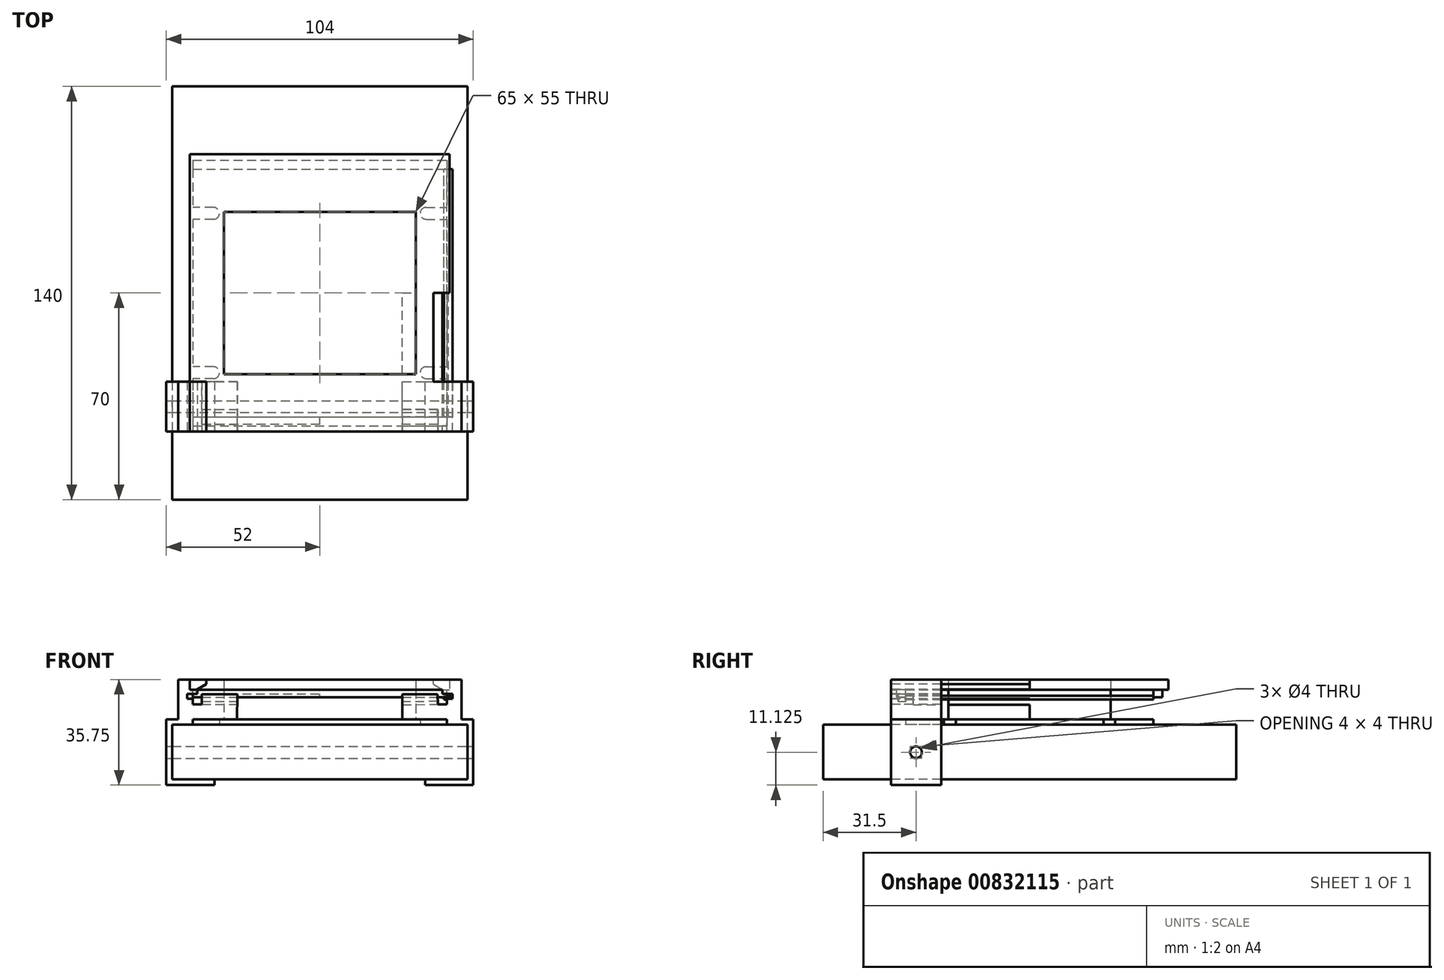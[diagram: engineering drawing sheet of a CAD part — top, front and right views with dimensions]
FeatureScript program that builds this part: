
annotation { "Feature Type Name" : "Feature", "Feature Type Description" : "" }
export const myFeature = defineFeature(function(context is Context, id is Id, definition is map)
    precondition{}
    {
        {
            var Q0;
            Q0=qCreatedBy(makeId("Top.planeOp"),FACE);
            var sketch = newSketch(context, id + "F0", { "sketchPlane" : qUnion([Q0])});
            skLineSegment(sketch, "E0.bottom", {"start": v(-50, -70) * mm, "end": v(50, -70) * mm});
            skLineSegment(sketch, "E0.top", {"start": v(-50, 70) * mm, "end": v(50, 70) * mm});
            skLineSegment(sketch, "E0.left", {"start": v(-50, -70) * mm, "end": v(-50, 70) * mm});
            skLineSegment(sketch, "E0.right", {"start": v(50, -70) * mm, "end": v(50, 70) * mm});
            skPoint(sketch, "E0.middle", {"position": v(0, 0) * mm});
            skSolve(sketch);
        }
        {
            var Q0;
            Q0=qSketchRegion(id+"F0",true);
            extrude(context, id + "F1", {"entities" : qUnion([Q0]), "oppositeDirection" : true, "depth" : 18.5 * mm});
        }
        {
            var Q0;
            Q0=qCreatedBy(makeId("Top.planeOp"),FACE);
            var sketch = newSketch(context, id + "F2", { "sketchPlane" : qUnion([Q0])});
            skLineSegment(sketch, "E1.bottom", {"start": v(-43, 42) * mm, "end": v(43, 42) * mm});
            skLineSegment(sketch, "E1.top", {"start": v(-43, -42) * mm, "end": v(43, -42) * mm});
            skLineSegment(sketch, "E1.left", {"start": v(-43, 42) * mm, "end": v(-43, 29) * mm});
            skLineSegment(sketch, "E1.right", {"start": v(43, 42) * mm, "end": v(43, 29) * mm});
            skPoint(sketch, "E1.middle", {"position": v(0, 0) * mm});
            skArc(sketch, "E2", {"start": v(-36, 25) * mm, "mid": v(-34, 27) * mm, "end": v(-36, 29) * mm});
            skLineSegment(sketch, "E3", {"start": v(-36, 25) * mm, "end": v(-43, 25) * mm});
            skLineSegment(sketch, "E4", {"start": v(-36, 29) * mm, "end": v(-43, 29) * mm});
            skArc(sketch, "E5.MirrorCS", {"start": v(36, 25) * mm, "mid": v(34, 27) * mm, "end": v(36, 29) * mm});
            skLineSegment(sketch, "E6.MirrorCS", {"start": v(36, 29) * mm, "end": v(43, 29) * mm});
            skLineSegment(sketch, "E7.MirrorCS", {"start": v(36, 25) * mm, "end": v(43, 25) * mm});
            skLineSegment(sketch, "E8.MirrorCS", {"start": v(-36, -25) * mm, "end": v(-43, -25) * mm});
            skLineSegment(sketch, "E9.MirrorCS", {"start": v(-36, -29) * mm, "end": v(-43, -29) * mm});
            skArc(sketch, "E10.MirrorCS", {"start": v(-36, -25) * mm, "mid": v(-34, -27) * mm, "end": v(-36, -29) * mm});
            skLineSegment(sketch, "E11.MirrorCS", {"start": v(36, -25) * mm, "end": v(43, -25) * mm});
            skLineSegment(sketch, "E12.MirrorCS", {"start": v(36, -29) * mm, "end": v(43, -29) * mm});
            skArc(sketch, "E13.MirrorCS", {"start": v(36, -25) * mm, "mid": v(34, -27) * mm, "end": v(36, -29) * mm});
            skLineSegment(sketch, "E14.trimOffspring", {"start": v(-43, 25) * mm, "end": v(-43, -25) * mm});
            skLineSegment(sketch, "E15.trimOffspring", {"start": v(-43, -29) * mm, "end": v(-43, -42) * mm});
            skLineSegment(sketch, "E16.trimOffspring", {"start": v(43, -29) * mm, "end": v(43, -42) * mm});
            skLineSegment(sketch, "E17.trimOffspring", {"start": v(43, 25) * mm, "end": v(43, -25) * mm});
            skSolve(sketch);
        }
        {
            var Q0;
            Q0=qSketchRegion(id+"F2",true);
            extrude(context, id + "F3", {"entities" : qUnion([Q0]), "depth" : 1.75 * mm});
        }
        {
            var Q0;
            Q0=makeQuery(id+"F3.opExtrude","CAP_FACE",FACE,{"disambiguationData":[OSD([sQuery(id+"F2.wireOp",EDGE,"E1.bottom"),sQuery(id+"F2.wireOp",EDGE,"E1.top"),sQuery(id+"F2.wireOp",EDGE,"E1.left"),sQuery(id+"F2.wireOp",EDGE,"E1.right"),sQuery(id+"F2.wireOp",EDGE,"E2"),sQuery(id+"F2.wireOp",EDGE,"E3"),sQuery(id+"F2.wireOp",EDGE,"E4"),sQuery(id+"F2.wireOp",EDGE,"E5.MirrorCS"),sQuery(id+"F2.wireOp",EDGE,"E6.MirrorCS"),sQuery(id+"F2.wireOp",EDGE,"E7.MirrorCS"),sQuery(id+"F2.wireOp",EDGE,"E8.MirrorCS"),sQuery(id+"F2.wireOp",EDGE,"E9.MirrorCS"),sQuery(id+"F2.wireOp",EDGE,"E10.MirrorCS"),sQuery(id+"F2.wireOp",EDGE,"E11.MirrorCS"),sQuery(id+"F2.wireOp",EDGE,"E12.MirrorCS"),sQuery(id+"F2.wireOp",EDGE,"E13.MirrorCS"),sQuery(id+"F2.wireOp",EDGE,"E14.trimOffspring"),sQuery(id+"F2.wireOp",EDGE,"E15.trimOffspring"),sQuery(id+"F2.wireOp",EDGE,"E16.trimOffspring"),sQuery(id+"F2.wireOp",EDGE,"E17.trimOffspring")])],"isStart":false});
            var sketch = newSketch(context, id + "F4", { "sketchPlane" : qUnion([Q0])});
            skLineSegment(sketch, "E18.bottom", {"start": v(-45, 47) * mm, "end": v(45, 47) * mm});
            skLineSegment(sketch, "E18.top", {"start": v(-45, -47) * mm, "end": v(45, -47) * mm});
            skLineSegment(sketch, "E18.left", {"start": v(-45, 47) * mm, "end": v(-45, -47) * mm});
            skLineSegment(sketch, "E18.right", {"start": v(45, 47) * mm, "end": v(45, -47) * mm});
            skPoint(sketch, "E18.middle", {"position": v(0, 0) * mm});
            skLineSegment(sketch, "E19.bottom", {"start": v(-43, 45) * mm, "end": v(43, 45) * mm});
            skLineSegment(sketch, "E19.top", {"start": v(-43, -45) * mm, "end": v(43, -45) * mm});
            skLineSegment(sketch, "E19.left", {"start": v(-43, 45) * mm, "end": v(-43, -45) * mm});
            skLineSegment(sketch, "E19.right", {"start": v(43, 45) * mm, "end": v(43, -45) * mm});
            skLineSegment(sketch, "E20", {"start": v(-43, 45) * mm, "end": v(-45, 45) * mm});
            skLineSegment(sketch, "E21", {"start": v(43, 45) * mm, "end": v(45, 45) * mm});
            skLineSegment(sketch, "E22.MirrorCS", {"start": v(-43, -45) * mm, "end": v(-45, -45) * mm});
            skLineSegment(sketch, "E23.MirrorCS", {"start": v(43, -45) * mm, "end": v(45, -45) * mm});
            skLineSegment(sketch, "E24", {"start": v(-43, 45) * mm, "end": v(-43, 47) * mm});
            skLineSegment(sketch, "E25.MirrorCS", {"start": v(43, 45) * mm, "end": v(43, 47) * mm});
            skLineSegment(sketch, "E26.MirrorCS", {"start": v(-43, -45) * mm, "end": v(-43, -47) * mm});
            skLineSegment(sketch, "E27.MirrorCS", {"start": v(43, -45) * mm, "end": v(43, -47) * mm});
            skLineSegment(sketch, "E28.bottom", {"start": v(-32.5, 27.5) * mm, "end": v(32.5, 27.5) * mm});
            skLineSegment(sketch, "E28.top", {"start": v(-32.5, -27.5) * mm, "end": v(32.5, -27.5) * mm});
            skLineSegment(sketch, "E28.left", {"start": v(-32.5, 27.5) * mm, "end": v(-32.5, -27.5) * mm});
            skLineSegment(sketch, "E28.right", {"start": v(32.5, 27.5) * mm, "end": v(32.5, -27.5) * mm});
            skSolve(sketch);
        }
        {
            var Q0;
            Q0=makeQuery(id+"F4.imprint","IMPRINT",FACE,{"disambiguationData":[TD([[makeQuery(id+"F4.imprint","IMPRINT",EDGE,{"derivedFrom":sQuery(id+"F4.wireOp",EDGE,"E28.bottom")}),-1.0]])]});
            extrude(context, id + "F5", {"entities" : qUnion([Q0]), "depth" : 10 * mm});
        }
        {
            var Q0;
            Q0=makeQuery(id+"F5.opExtrude","CAP_FACE",FACE,{"disambiguationData":[OSD([sQuery(id+"F4.wireOp",EDGE,"E28.bottom"),sQuery(id+"F4.wireOp",EDGE,"E28.top"),sQuery(id+"F4.wireOp",EDGE,"E28.left"),sQuery(id+"F4.wireOp",EDGE,"E28.right")])],"isStart":false});
            var sketch = newSketch(context, id + "F6", { "sketchPlane" : qUnion([Q0])});
            skLineSegment(sketch, "E29.bottom", {"start": v(-44, 47) * mm, "end": v(44, 47) * mm});
            skLineSegment(sketch, "E29.top", {"start": v(-44, -47) * mm, "end": v(44, -47) * mm});
            skLineSegment(sketch, "E29.left", {"start": v(-44, 47) * mm, "end": v(-44, -47) * mm});
            skLineSegment(sketch, "E29.right", {"start": v(44, 47) * mm, "end": v(44, -47) * mm});
            skPoint(sketch, "E29.middle", {"position": v(0, 0) * mm});
            skLineSegment(sketch, "E30.bottom", {"start": v(-43, 45) * mm, "end": v(43, 45) * mm});
            skLineSegment(sketch, "E30.top", {"start": v(-43, -45) * mm, "end": v(43, -45) * mm});
            skLineSegment(sketch, "E30.left", {"start": v(-43, 45) * mm, "end": v(-43, -45) * mm});
            skLineSegment(sketch, "E30.right", {"start": v(43, 45) * mm, "end": v(43, -45) * mm});
            skLineSegment(sketch, "E31.MirrorCS", {"start": v(-43, -44) * mm, "end": v(-43, -45) * mm});
            skLineSegment(sketch, "E32.MirrorCS", {"start": v(43, -44) * mm, "end": v(43, -45) * mm});
            skLineSegment(sketch, "E33.bottom", {"start": v(-32.5, 27.5) * mm, "end": v(32.5, 27.5) * mm});
            skLineSegment(sketch, "E33.top", {"start": v(-32.5, -27.5) * mm, "end": v(32.5, -27.5) * mm});
            skLineSegment(sketch, "E33.left", {"start": v(-32.5, 27.5) * mm, "end": v(-32.5, -27.5) * mm});
            skLineSegment(sketch, "E33.right", {"start": v(32.5, 27.5) * mm, "end": v(32.5, -27.5) * mm});
            skLineSegment(sketch, "E34.0", {"start": v(-43, 42) * mm, "end": v(43, 42) * mm});
            skLineSegment(sketch, "E35.0", {"start": v(-43, -42) * mm, "end": v(43, -42) * mm});
            skSolve(sketch);
        }
        {
            var Q0;
            Q0=makeQuery(id+"F6.imprint","IMPRINT",FACE,{"disambiguationData":[TD([[makeQuery(id+"F6.imprint","IMPRINT",EDGE,{"derivedFrom":sQuery(id+"F6.wireOp",EDGE,"E30.bottom")}),1.0]])]});
            var Q1;
            {var subQ0=sQuery(id+"F6.wireOp",EDGE,"E30.bottom");Q1=makeQuery(id+"F6.imprint","IMPRINT",FACE,{"disambiguationData":[TD([[makeQuery(id+"F6.imprint","IMPRINT",EDGE,{"derivedFrom":subQ0}),-1.0]])]});}
            var Q2;
            Q2=makeQuery(id+"F6.imprint","IMPRINT",FACE,{"disambiguationData":[TD([[makeQuery(id+"F6.imprint","IMPRINT",EDGE,{"derivedFrom":sQuery(id+"F6.wireOp",EDGE,"E33.bottom")}),1.0]])]});
            var Q3;
            {var subQ0=sQuery(id+"F6.wireOp",EDGE,"E30.top");Q3=makeQuery(id+"F6.imprint","IMPRINT",FACE,{"disambiguationData":[TD([[makeQuery(id+"F6.imprint","IMPRINT",EDGE,{"derivedFrom":subQ0}),1.0]])]});}
            var Q4;
            Q4=makeQuery(id+"F6.imprint","IMPRINT",FACE,{"disambiguationData":[TD([[makeQuery(id+"F6.imprint","IMPRINT",EDGE,{"derivedFrom":sQuery(id+"F6.wireOp",EDGE,"E30.top")}),-1.0]])]});
            extrude(context, id + "F7", {"entities" : qUnion([Q0, Q1, Q2, Q3, Q4]), "depth" : 3.5 * mm});
        }
        {
            var Q0;
            {var subQ0=sQuery(id+"F6.wireOp",EDGE,"E30.bottom");Q0=makeQuery(id+"F6.imprint","IMPRINT",FACE,{"disambiguationData":[TD([[makeQuery(id+"F6.imprint","IMPRINT",EDGE,{"derivedFrom":subQ0}),-1.0]])]});}
            var Q1;
            {var subQ0=sQuery(id+"F6.wireOp",EDGE,"E30.top");Q1=makeQuery(id+"F6.imprint","IMPRINT",FACE,{"disambiguationData":[TD([[makeQuery(id+"F6.imprint","IMPRINT",EDGE,{"derivedFrom":subQ0}),1.0]])]});}
            extrude(context, id + "F8", {"entities" : qUnion([Q0, Q1]), "operationType" : NewBodyOperationType.ADD, "oppositeDirection" : true, "depth" : 2.5 * mm});
        }
        {
            var Q0;
            Q0=qCreatedBy(makeId("Front.planeOp"),FACE);
            var sketch = newSketch(context, id + "F9", { "sketchPlane" : qUnion([Q0])});
            skLineSegment(sketch, "E36.0", {"start": v(43, 13.75) * mm, "end": v(43, 10.25) * mm});
            skLineSegment(sketch, "E37.0", {"start": v(43, 13.75) * mm, "end": v(43, 9.75) * mm});
            skLineSegment(sketch, "E38.0", {"start": v(43, 7.25) * mm, "end": v(43, 9.75) * mm});
            skLineSegment(sketch, "E39", {"start": v(43, 9.75) * mm, "end": v(43, 8.5) * mm});
            skLineSegment(sketch, "E40", {"start": v(43, 8.5) * mm, "end": v(45, 9.75) * mm});
            skLineSegment(sketch, "E41", {"start": v(45, 9.75) * mm, "end": v(43, 9.75) * mm});
            skLineSegment(sketch, "E42.bottom", {"start": v(43, 9.75) * mm, "end": v(42, 9.75) * mm});
            skLineSegment(sketch, "E42.top", {"start": v(43, 8.5) * mm, "end": v(42, 8.5) * mm});
            skLineSegment(sketch, "E42.right", {"start": v(42, 9.75) * mm, "end": v(42, 8.5) * mm});
            skSolve(sketch);
        }
        {
            var Q0;
            Q0=qSketchRegion(id+"F9",true);
            extrude(context, id + "F10", {"entities" : qUnion([Q0]), "operationType" : NewBodyOperationType.ADD, "depth" : 42 * mm, "hasSecondDirection" : true, "secondDirectionOppositeDirection" : true, "secondDirectionDepth" : 42 * mm});
        }
        {
            var Q0;
            Q0=qCreatedBy(makeId("Front.planeOp"),FACE);
            var sketch = newSketch(context, id + "F11", { "sketchPlane" : qUnion([Q0])});
            skLineSegment(sketch, "E43.0", {"start": v(28, 1.75) * mm, "end": v(43, 1.75) * mm});
            skLineSegment(sketch, "E44.0", {"start": v(43, 1.75) * mm, "end": v(43, 0) * mm});
            skLineSegment(sketch, "E45", {"start": v(43, 0) * mm, "end": v(48, 0) * mm});
            skPoint(sketch, "E46.orphan", {"position": v(43, 9.75) * mm});
            skPoint(sketch, "E47.orphan", {"position": v(-43, 9.25) * mm});
            skPoint(sketch, "E48.orphan", {"position": v(-43, 1.75) * mm});
            skPoint(sketch, "E49.end.orphan", {"position": v(43, 7.25) * mm});
            skLineSegment(sketch, "E50", {"start": v(27.97, 6.75) * mm, "end": v(28, 1.75) * mm});
            skLineSegment(sketch, "E51", {"start": v(48, 13.75) * mm, "end": v(48, 1.75) * mm});
            skPoint(sketch, "E52.0.end.orphan", {"position": v(45, 9.75) * mm});
            skLineSegment(sketch, "E53.0", {"start": v(45, 9.75) * mm, "end": v(43, 9.75) * mm, "construction": true});
            skLineSegment(sketch, "E54.0", {"start": v(43, 8.5) * mm, "end": v(45, 9.75) * mm, "construction": true});
            skLineSegment(sketch, "E55", {"start": v(27.97, 6.75) * mm, "end": v(43, 6.84) * mm});
            skLineSegment(sketch, "E56.bottom", {"start": v(43, 0) * mm, "end": v(52, 0) * mm});
            skLineSegment(sketch, "E56.top", {"start": v(48, 1.75) * mm, "end": v(52, 1.75) * mm});
            skLineSegment(sketch, "E56.left", {"start": v(43, 0) * mm, "end": v(43, 1.75) * mm});
            skLineSegment(sketch, "E57.right", {"start": v(41.5, 11.88) * mm, "end": v(41.5, 10.45) * mm});
            skLineSegment(sketch, "E58", {"start": v(38.5, 13.75) * mm, "end": v(41.5, 11.88) * mm});
            skLineSegment(sketch, "E59", {"start": v(41.5, 10.45) * mm, "end": v(44.97, 10.45) * mm});
            skLineSegment(sketch, "E60", {"start": v(44.97, 10.45) * mm, "end": v(45, 8.79) * mm});
            skLineSegment(sketch, "E61", {"start": v(45, 8.79) * mm, "end": v(43, 8.75) * mm});
            skPoint(sketch, "E62.orphan", {"position": v(43, 10) * mm});
            skPoint(sketch, "E63.orphan", {"position": v(41.5, 10) * mm});
            skLineSegment(sketch, "E64", {"start": v(43, 8.75) * mm, "end": v(43, 6.84) * mm});
            skLineSegment(sketch, "E65.top", {"start": v(38.5, 15.25) * mm, "end": v(48, 15.25) * mm});
            skLineSegment(sketch, "E65.left", {"start": v(38.5, 13.75) * mm, "end": v(38.5, 15.25) * mm});
            skLineSegment(sketch, "E65.right", {"start": v(48, 13.75) * mm, "end": v(48, 15.25) * mm});
            skPoint(sketch, "E57.bottom.end.orphan", {"position": v(41.5, 13.75) * mm});
            skLineSegment(sketch, "E66.0", {"start": v(50, -18.5) * mm, "end": v(50, 0) * mm});
            skLineSegment(sketch, "E67.0", {"start": v(-50, -18.5) * mm, "end": v(50, -18.5) * mm});
            skLineSegment(sketch, "E68", {"start": v(48, 0) * mm, "end": v(50, 0) * mm});
            skLineSegment(sketch, "E69", {"start": v(50, -18.5) * mm, "end": v(35.7, -18.5) * mm});
            skLineSegment(sketch, "E70", {"start": v(35.7, -18.5) * mm, "end": v(35.7, -20.5) * mm});
            skLineSegment(sketch, "E71", {"start": v(35.7, -20.5) * mm, "end": v(52, -20.5) * mm});
            skLineSegment(sketch, "E72", {"start": v(52, -20.5) * mm, "end": v(52, 1.75) * mm});
            skPoint(sketch, "E56.right.end.orphan", {"position": v(63, 1.75) * mm});
            skSolve(sketch);
        }
        {
            var Q0;
            Q0=qSketchRegion(id+"F11",true);
            extrude(context, id + "F12", {"entities" : qUnion([Q0]), "depth" : 47 * mm});
        }
        {
            var Q0;
            Q0=qSketchRegion(id+"F11",true);
            extrude(context, id + "F13", {"entities" : qUnion([Q0]), "operationType" : NewBodyOperationType.REMOVE, "depth" : 30 * mm});
        }
        {
            var Q0;
            Q0=makeQuery(id+"F12.opExtrude","SWEPT_FACE",FACE,{"disambiguationData":[OSD([sQuery(id+"F11.wireOp",EDGE,"E50")])]});
            var sketch = newSketch(context, id + "F14", { "sketchPlane" : qUnion([Q0])});
            skPoint(sketch, "E73.right.end.orphan", {"position": v(-45, -81.5) * mm});
            skPoint(sketch, "E74.0.end.orphan", {"position": v(42, 12) * mm});
            skPoint(sketch, "E74.0.start.orphan", {"position": v(-42, 9.5) * mm});
            skPoint(sketch, "E75.0.end.orphan", {"position": v(-45, 12) * mm});
            skPoint(sketch, "E75.0.start.orphan", {"position": v(-45, 9.5) * mm});
            skPoint(sketch, "E76.0.end.orphan", {"position": v(-45, 9.08) * mm});
            skPoint(sketch, "E76.0.start.orphan", {"position": v(42, 7.08) * mm});
            skPoint(sketch, "E77.0.3.end.orphan", {"position": v(47, 6.58) * mm});
            skPoint(sketch, "E77.0.3.start.orphan", {"position": v(47, 6.58) * mm});
            skPoint(sketch, "E77.0.1.end.orphan", {"position": v(30, 6.58) * mm});
            skPoint(sketch, "E77.0.1.start.orphan", {"position": v(30, 6.58) * mm});
            skLineSegment(sketch, "E78.0", {"start": v(-45, 9.5) * mm, "end": v(-45, 12) * mm, "construction": true});
            skLineSegment(sketch, "E79.0", {"start": v(42, 8.25) * mm, "end": v(42, 9.58) * mm, "construction": true});
            skLineSegment(sketch, "E80.0", {"start": v(-45, 12) * mm, "end": v(-46, 12) * mm, "construction": true});
            skLineSegment(sketch, "E81.0", {"start": v(-45, 12) * mm, "end": v(-135, 12) * mm, "construction": true});
            skLineSegment(sketch, "E82.top", {"start": v(47, 5.94) * mm, "end": v(39.5, 5.94) * mm});
            skPoint(sketch, "E83.orphan", {"position": v(39.5, 7.08) * mm});
            skLineSegment(sketch, "E84", {"start": v(-45, 11.58) * mm, "end": v(-45, 9.08) * mm});
            skLineSegment(sketch, "E85", {"start": v(47, 10.08) * mm, "end": v(47, 5.94) * mm});
            skPoint(sketch, "E86.orphan", {"position": v(-42, 8.25) * mm});
            skLineSegment(sketch, "E87.right", {"start": v(47, 10.08) * mm, "end": v(47, 7.08) * mm});
            skPoint(sketch, "E88.orphan", {"position": v(45, 12) * mm});
            skPoint(sketch, "E89.0.start.orphan", {"position": v(45, 9.5) * mm});
            skLineSegment(sketch, "E90", {"start": v(44.5, 10.08) * mm, "end": v(44.5, 7.58) * mm});
            skLineSegment(sketch, "E91", {"start": v(42, 7.58) * mm, "end": v(42, 9.58) * mm});
            skLineSegment(sketch, "E92", {"start": v(39.5, 9.58) * mm, "end": v(39.5, 5.94) * mm});
            skLineSegment(sketch, "E93", {"start": v(42, 7.58) * mm, "end": v(44.5, 7.58) * mm});
            skLineSegment(sketch, "E94.top", {"start": v(42, 10.08) * mm, "end": v(39.5, 10.08) * mm});
            skLineSegment(sketch, "E94.left", {"start": v(42, 9.58) * mm, "end": v(42, 10.08) * mm});
            skLineSegment(sketch, "E94.right", {"start": v(39.5, 9.58) * mm, "end": v(39.5, 10.08) * mm});
            skLineSegment(sketch, "E95", {"start": v(44.5, 10.08) * mm, "end": v(47, 10.08) * mm});
            skSolve(sketch);
        }
        {
            var Q0;
            Q0=qSketchRegion(id+"F14",true);
            extrude(context, id + "F15", {"entities" : qUnion([Q0]), "operationType" : NewBodyOperationType.ADD, "oppositeDirection" : true, "depth" : 12 * mm});
        }
        {
            var Q0;
            Q0=makeQuery(id+"F15.boolean.opBoolean","MERGE",FACE,{"derivedFrom":[makeQuery(id+"F12.opExtrude","CAP_FACE",FACE,{"disambiguationData":[OSD([sQuery(id+"F11.wireOp",EDGE,"E43.0"),sQuery(id+"F11.wireOp",EDGE,"E50"),sQuery(id+"F11.wireOp",EDGE,"E51"),sQuery(id+"F11.wireOp",EDGE,"E55"),sQuery(id+"F11.wireOp",EDGE,"E56.bottom"),sQuery(id+"F11.wireOp",EDGE,"E56.top"),sQuery(id+"F11.wireOp",EDGE,"E56.left"),sQuery(id+"F11.wireOp",EDGE,"E57.right"),sQuery(id+"F11.wireOp",EDGE,"E58"),sQuery(id+"F11.wireOp",EDGE,"E59"),sQuery(id+"F11.wireOp",EDGE,"E60"),sQuery(id+"F11.wireOp",EDGE,"E61"),sQuery(id+"F11.wireOp",EDGE,"E64"),sQuery(id+"F11.wireOp",EDGE,"E65.top"),sQuery(id+"F11.wireOp",EDGE,"E65.left"),sQuery(id+"F11.wireOp",EDGE,"E65.right"),sQuery(id+"F11.wireOp",EDGE,"E66.0"),sQuery(id+"F11.wireOp",EDGE,"E68"),sQuery(id+"F11.wireOp",EDGE,"E69"),sQuery(id+"F11.wireOp",EDGE,"E70"),sQuery(id+"F11.wireOp",EDGE,"E71"),sQuery(id+"F11.wireOp",EDGE,"E72")])],"isStart":false}),makeQuery(id+"F15.opExtrude","SWEPT_FACE",FACE,{"disambiguationData":[OSD([sQuery(id+"F14.wireOp",EDGE,"E85"),sQuery(id+"F14.wireOp",EDGE,"E87.right")])]})]});
            var sketch = newSketch(context, id + "F16", { "sketchPlane" : qUnion([Q0])});
            skLineSegment(sketch, "E96.MirrorCS", {"start": v(-35.7, -18.5) * mm, "end": v(-35.7, -20.5) * mm});
            skLineSegment(sketch, "E97.MirrorCS", {"start": v(-38.5, 13.75) * mm, "end": v(-41.5, 11.88) * mm});
            skLineSegment(sketch, "E98.MirrorCS", {"start": v(-38.5, 15.25) * mm, "end": v(-38.5, 13.75) * mm});
            skLineSegment(sketch, "E99.MirrorCS", {"start": v(-41.5, 11.88) * mm, "end": v(-41.5, 10.45) * mm});
            skLineSegment(sketch, "E100.MirrorCS", {"start": v(-44.97, 10.45) * mm, "end": v(-45, 8.79) * mm});
            skLineSegment(sketch, "E101.MirrorCS", {"start": v(-43, 8.75) * mm, "end": v(-43, 6.84) * mm});
            skLineSegment(sketch, "E102.MirrorCS", {"start": v(-41.5, 10.45) * mm, "end": v(-44.97, 10.45) * mm});
            skLineSegment(sketch, "E103.MirrorCS", {"start": v(-45, 8.79) * mm, "end": v(-43, 8.75) * mm});
            skLineSegment(sketch, "E104.MirrorCS", {"start": v(-43, 1.75) * mm, "end": v(-43, 0) * mm});
            skLineSegment(sketch, "E105.MirrorCS", {"start": v(-43, 6.84) * mm, "end": v(-39.97, 6.82) * mm});
            skLineSegment(sketch, "E106.MirrorCS", {"start": v(-35.7, -20.5) * mm, "end": v(-52, -20.5) * mm});
            skLineSegment(sketch, "E107.MirrorCS", {"start": v(-39.95, 10.32) * mm, "end": v(-27.95, 10.25) * mm});
            skLineSegment(sketch, "E108.MirrorCS", {"start": v(-48, 15.25) * mm, "end": v(-38.5, 15.25) * mm});
            skLineSegment(sketch, "E109.MirrorCS", {"start": v(-39.97, 6.82) * mm, "end": v(-39.95, 10.32) * mm});
            skLineSegment(sketch, "E110.MirrorCS", {"start": v(-48, 1.75) * mm, "end": v(-48, 15.25) * mm});
            skLineSegment(sketch, "E111.MirrorCS", {"start": v(-52, 1.75) * mm, "end": v(-48, 1.75) * mm});
            skLineSegment(sketch, "E112.MirrorCS", {"start": v(-52, -20.5) * mm, "end": v(-52, 1.75) * mm});
            skLineSegment(sketch, "E113.MirrorCS", {"start": v(-50, -18.5) * mm, "end": v(-35.7, -18.5) * mm});
            skLineSegment(sketch, "E114.MirrorCS", {"start": v(-50, 0) * mm, "end": v(-50, -18.5) * mm});
            skLineSegment(sketch, "E115.MirrorCS", {"start": v(-43, 0) * mm, "end": v(-50, 0) * mm});
            skLineSegment(sketch, "E116.MirrorCS", {"start": v(-28, 1.75) * mm, "end": v(-43, 1.75) * mm});
            skLineSegment(sketch, "E117.MirrorCS", {"start": v(-27.95, 10.25) * mm, "end": v(-28, 1.75) * mm});
            skSolve(sketch);
        }
        {
            var Q0;
            Q0=qSketchRegion(id+"F16",true);
            extrude(context, id + "F17", {"entities" : qUnion([Q0]), "oppositeDirection" : true, "depth" : 17 * mm});
        }
        {
            var Q0;
            Q0=qCreatedBy(makeId("Right.planeOp"),FACE);
            var sketch = newSketch(context, id + "F18", { "sketchPlane" : qUnion([Q0])});
            skLineSegment(sketch, "E118.0.2", {"start": v(-44.5, 10.25) * mm, "end": v(-44.5, 7.82) * mm});
            skLineSegment(sketch, "E118.0.4", {"start": v(-42, 7.82) * mm, "end": v(-42, 10.25) * mm});
            skLineSegment(sketch, "E118.0.6", {"start": v(-39.5, 10.25) * mm, "end": v(-39.5, 6.84) * mm});
            skLineSegment(sketch, "E119.0.2", {"start": v(-30, 6.84) * mm, "end": v(-30, 10.25) * mm});
            skPoint(sketch, "E118.0.0.end.orphan", {"position": v(-47, 10.25) * mm});
            skPoint(sketch, "E118.0.9.start.orphan", {"position": v(-30, 1.75) * mm});
            skLineSegment(sketch, "E120.0", {"start": v(-39.5, 10.25) * mm, "end": v(-42, 10.25) * mm, "construction": true});
            skLineSegment(sketch, "E121.0", {"start": v(-30, 10.45) * mm, "end": v(-47, 10.45) * mm, "construction": true});
            skLineSegment(sketch, "E122.top", {"start": v(-44.5, 10.45) * mm, "end": v(-42, 10.45) * mm});
            skLineSegment(sketch, "E122.left", {"start": v(-44.5, 10.25) * mm, "end": v(-44.5, 10.45) * mm});
            skLineSegment(sketch, "E122.right", {"start": v(-42, 10.25) * mm, "end": v(-42, 10.45) * mm});
            skLineSegment(sketch, "E123.top", {"start": v(-39.5, 10.45) * mm, "end": v(-30, 10.45) * mm});
            skLineSegment(sketch, "E123.left", {"start": v(-39.5, 10.25) * mm, "end": v(-39.5, 10.45) * mm});
            skLineSegment(sketch, "E123.right", {"start": v(-30, 10.25) * mm, "end": v(-30, 10.45) * mm});
            skLineSegment(sketch, "E124.0", {"start": v(-39.5, 6.84) * mm, "end": v(-30, 6.84) * mm});
            skLineSegment(sketch, "E125.0", {"start": v(-42, 7.82) * mm, "end": v(-44.5, 7.82) * mm});
            skPoint(sketch, "E126.orphan", {"position": v(-30, 6.75) * mm});
            skPoint(sketch, "E127.orphan", {"position": v(-39.5, 6.75) * mm});
            skPoint(sketch, "E128.orphan", {"position": v(-47, 6.84) * mm});
            skPoint(sketch, "E129.orphan", {"position": v(-42, 7.75) * mm});
            skPoint(sketch, "E130.orphan", {"position": v(-44.5, 7.75) * mm});
            skSolve(sketch);
        }
        {
            var Q0;
            Q0=makeQuery(id+"F18.imprint","IMPRINT",FACE,{"disambiguationData":[TD([[makeQuery(id+"F18.imprint","IMPRINT",EDGE,{"derivedFrom":sQuery(id+"F18.wireOp",EDGE,"E118.0.6")}),1.0]])]});
            var Q1;
            Q1=makeQuery(id+"F18.imprint","IMPRINT",FACE,{"disambiguationData":[TD([[makeQuery(id+"F18.imprint","IMPRINT",EDGE,{"derivedFrom":sQuery(id+"F18.wireOp",EDGE,"E118.0.2")}),1.0]])]});
            extrude(context, id + "F19", {"entities" : qUnion([Q0, Q1]), "operationType" : NewBodyOperationType.REMOVE, "oppositeDirection" : true, "depth" : 40 * mm});
        }
        {
            var Q0;
            Q0=makeQuery(id+"F12.opExtrude","SWEPT_FACE",FACE,{"disambiguationData":[OSD([sQuery(id+"F11.wireOp",EDGE,"E72")])]});
            var sketch = newSketch(context, id + "F20", { "sketchPlane" : qUnion([Q0])});
            skCircle(sketch, "E131", {"center": v(-38.5, -9.38) * mm, "radius": 2 * mm});
            skPoint(sketch, "E131.centerSnap0", {"position": v(-47, -9.38) * mm});
            skPoint(sketch, "E131.centerSnap1", {"position": v(-38.5, 1.75) * mm});
            skSolve(sketch);
        }
        {
            var Q0;
            Q0=qSketchRegion(id+"F20",true);
            extrude(context, id + "F21", {"entities" : qUnion([Q0]), "operationType" : NewBodyOperationType.REMOVE, "oppositeDirection" : true, "depth" : 120 * mm});
        }
    });
